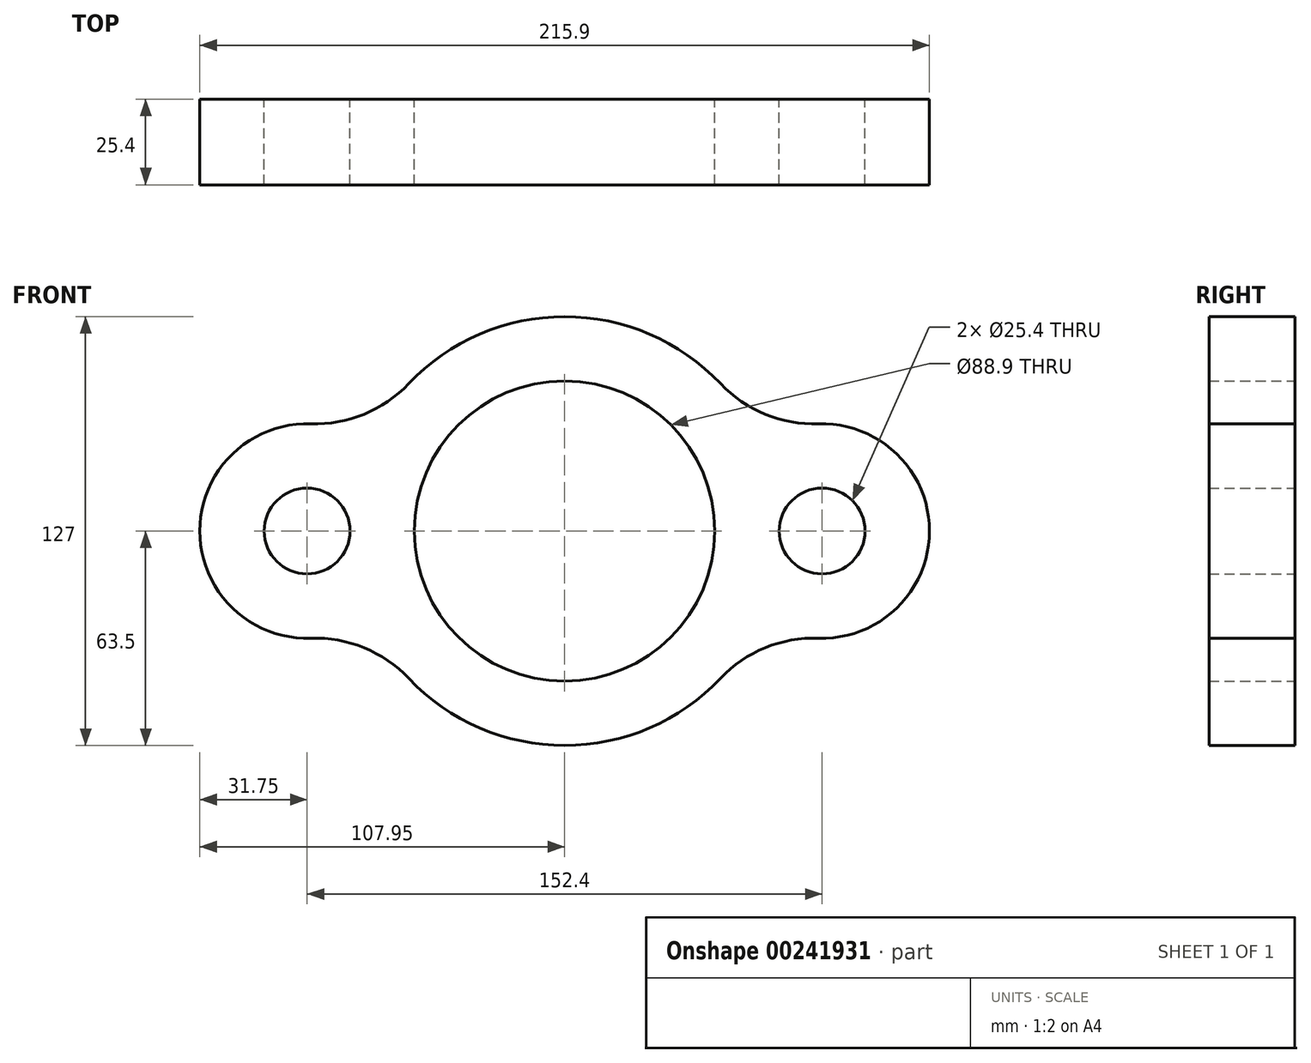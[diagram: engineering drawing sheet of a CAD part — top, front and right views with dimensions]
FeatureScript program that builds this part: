
annotation { "Feature Type Name" : "Feature", "Feature Type Description" : "" }
export const myFeature = defineFeature(function(context is Context, id is Id, definition is map)
    precondition{}
    {
        {
            var Q0;
            Q0=qCreatedBy(makeId("Front.planeOp"),FACE);
            var sketch = newSketch(context, id + "F0", { "sketchPlane" : qUnion([Q0])});
            skCircle(sketch, "E0", {"center": v(0, 0) * mm, "radius": 44.45 * mm});
            skArc(sketch, "E1", {"start": v(75.12, -31.73) * mm, "mid": v(107.95, 0) * mm, "end": v(75.12, 31.73) * mm});
            skArc(sketch, "E2", {"start": v(-75.12, 31.73) * mm, "mid": v(-107.95, 0) * mm, "end": v(-75.12, -31.73) * mm});
            skCircle(sketch, "E3", {"center": v(-76.2, 0) * mm, "radius": 12.7 * mm});
            skCircle(sketch, "E4", {"center": v(76.2, 0) * mm, "radius": 12.7 * mm});
            skArc(sketch, "E5.trimOffspring", {"start": v(-46.14, -43.63) * mm, "mid": v(0, -63.5) * mm, "end": v(46.14, -43.63) * mm});
            skPoint(sketch, "E6.visualSharp", {"position": v(-57.94, 25.98) * mm});
            skArc(sketch, "E6.filletArc", {"start": v(-75.12, 31.73) * mm, "mid": v(-59.35, 34.56) * mm, "end": v(-46.14, 43.63) * mm});
            skArc(sketch, "E7.trimOffspring", {"start": v(46.14, 43.63) * mm, "mid": v(0, 63.5) * mm, "end": v(-46.14, 43.63) * mm});
            skPoint(sketch, "E8.visualSharp", {"position": v(-57.94, -25.98) * mm});
            skArc(sketch, "E8.filletArc", {"start": v(-46.14, -43.63) * mm, "mid": v(-59.35, -34.56) * mm, "end": v(-75.12, -31.73) * mm});
            skPoint(sketch, "E9.visualSharp", {"position": v(57.94, -25.98) * mm});
            skArc(sketch, "E9.filletArc", {"start": v(75.12, -31.73) * mm, "mid": v(59.35, -34.56) * mm, "end": v(46.14, -43.63) * mm});
            skPoint(sketch, "E10.visualSharp", {"position": v(57.94, 25.98) * mm});
            skArc(sketch, "E10.filletArc", {"start": v(46.14, 43.63) * mm, "mid": v(59.35, 34.56) * mm, "end": v(75.12, 31.73) * mm});
            skSolve(sketch);
        }
        {
            var Q0;
            Q0 = qSketchRegion(id + "F0", true);
            extrude(context, id + "F1", {"entities" : qUnion([Q0]), "depth" : 25.4 * mm});
        }
    });
